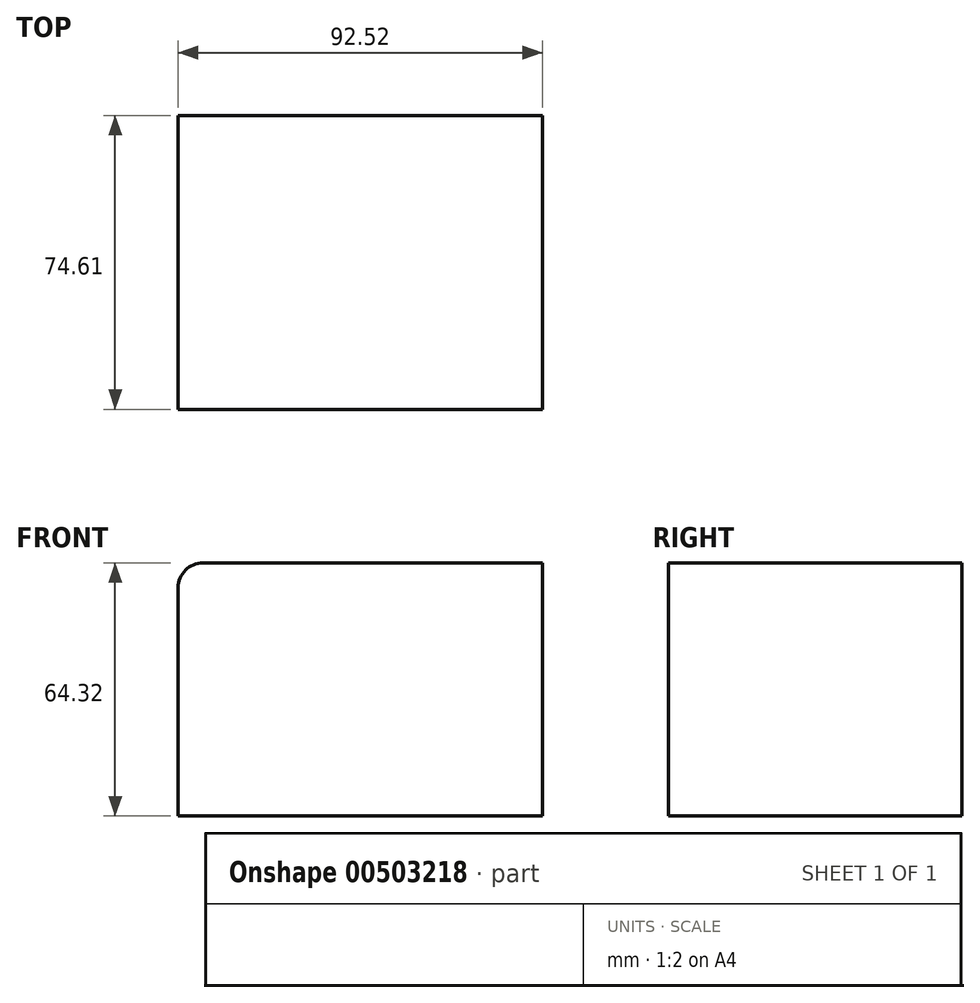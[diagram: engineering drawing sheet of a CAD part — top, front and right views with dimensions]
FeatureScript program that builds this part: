
annotation { "Feature Type Name" : "Feature", "Feature Type Description" : "" }
export const myFeature = defineFeature(function(context is Context, id is Id, definition is map)
    precondition{}
    {
        {
            var Q0;
            Q0=qCreatedBy(makeId("Front.planeOp"),FACE);
            var sketch = newSketch(context, id + "F0", { "sketchPlane" : qUnion([Q0])});
            skLineSegment(sketch, "E0.bottom", {"start": v(46.26, 32.16) * mm, "end": v(-39.91, 32.16) * mm});
            skLineSegment(sketch, "E0.top", {"start": v(46.26, -32.16) * mm, "end": v(-46.26, -32.16) * mm});
            skLineSegment(sketch, "E0.left", {"start": v(46.26, 32.16) * mm, "end": v(46.26, -32.16) * mm});
            skLineSegment(sketch, "E0.right", {"start": v(-46.26, 25.8) * mm, "end": v(-46.26, -32.16) * mm});
            skPoint(sketch, "E0.middle", {"position": v(0, 0) * mm});
            skPoint(sketch, "E1.visualSharp", {"position": v(-46.26, 32.16) * mm});
            skArc(sketch, "E1.filletArc", {"start": v(-39.91, 32.16) * mm, "mid": v(-44.4, 30.3) * mm, "end": v(-46.26, 25.8) * mm});
            skSolve(sketch);
        }
        {
            var Q0;
            Q0=makeQuery(id+"F0.imprint","IMPRINT",FACE,{"disambiguationData":[TD([[makeQuery(id+"F0.imprint","IMPRINT",EDGE,{"derivedFrom":sQuery(id+"F0.wireOp",EDGE,"E0.bottom")}),1.0]])]});
            extrude(context, id + "F1", {"entities" : qUnion([Q0]), "depth" : 74.6 * mm});
        }
    });
